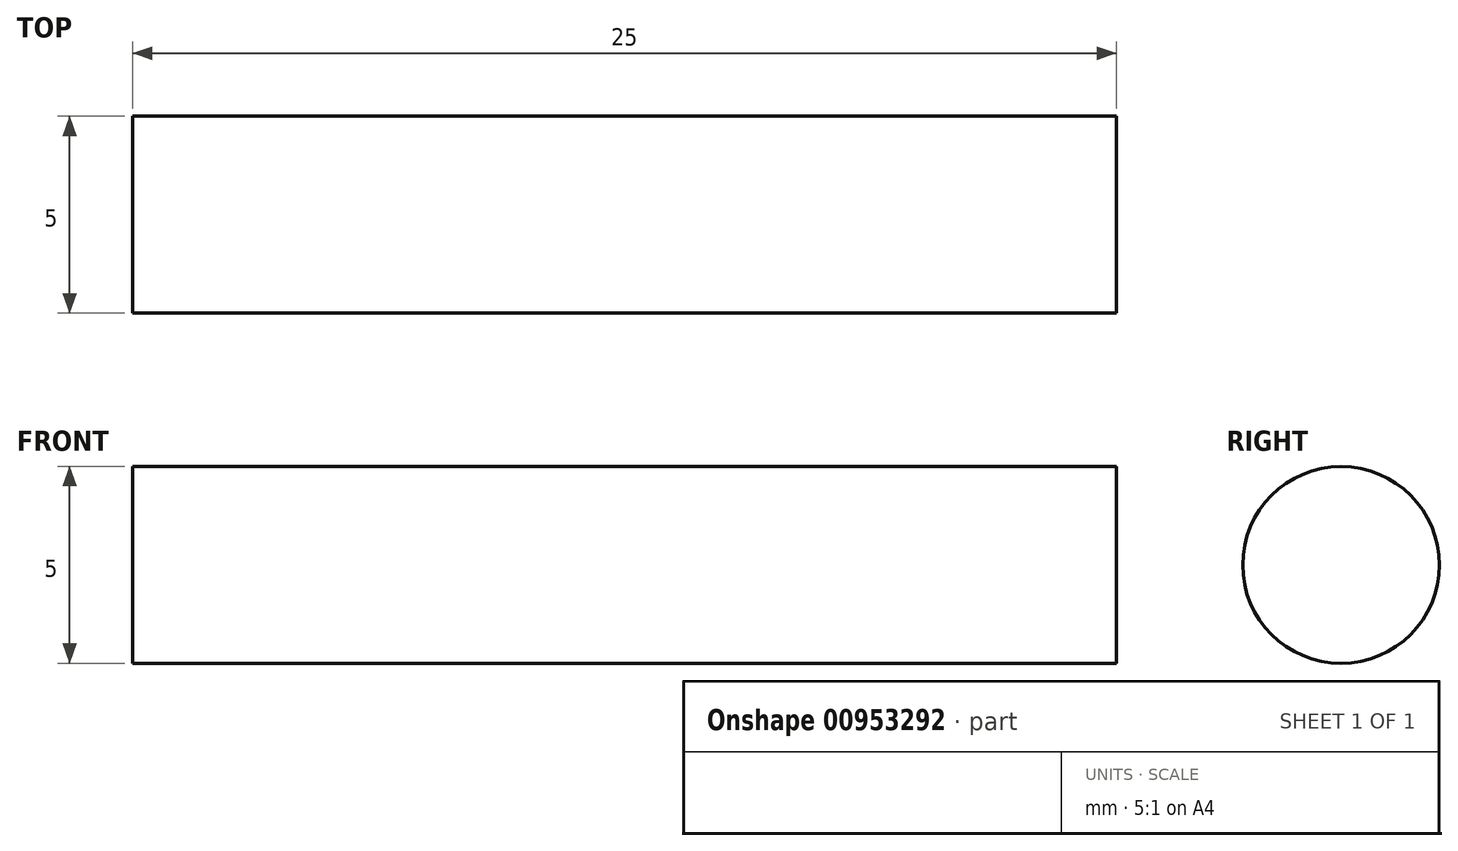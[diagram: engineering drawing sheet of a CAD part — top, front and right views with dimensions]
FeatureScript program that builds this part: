
annotation { "Feature Type Name" : "Feature", "Feature Type Description" : "" }
export const myFeature = defineFeature(function(context is Context, id is Id, definition is map)
    precondition{}
    {
        {
            var Q0;
            Q0=qCreatedBy(makeId("Right.planeOp"),FACE);
            var sketch = newSketch(context, id + "F0", { "sketchPlane" : qUnion([Q0])});
            skCircle(sketch, "E0", {"center": v(-6.5, 16.69) * mm, "radius": 2.5 * mm});
            skSolve(sketch);
        }
        {
            var Q0;
            Q0 = qSketchRegion(id + "F0", true);
            extrude(context, id + "F1", {"entities" : qUnion([Q0]), "depth" : 25 * mm, "offsetDistance" : 25 * mm});
        }
    });
